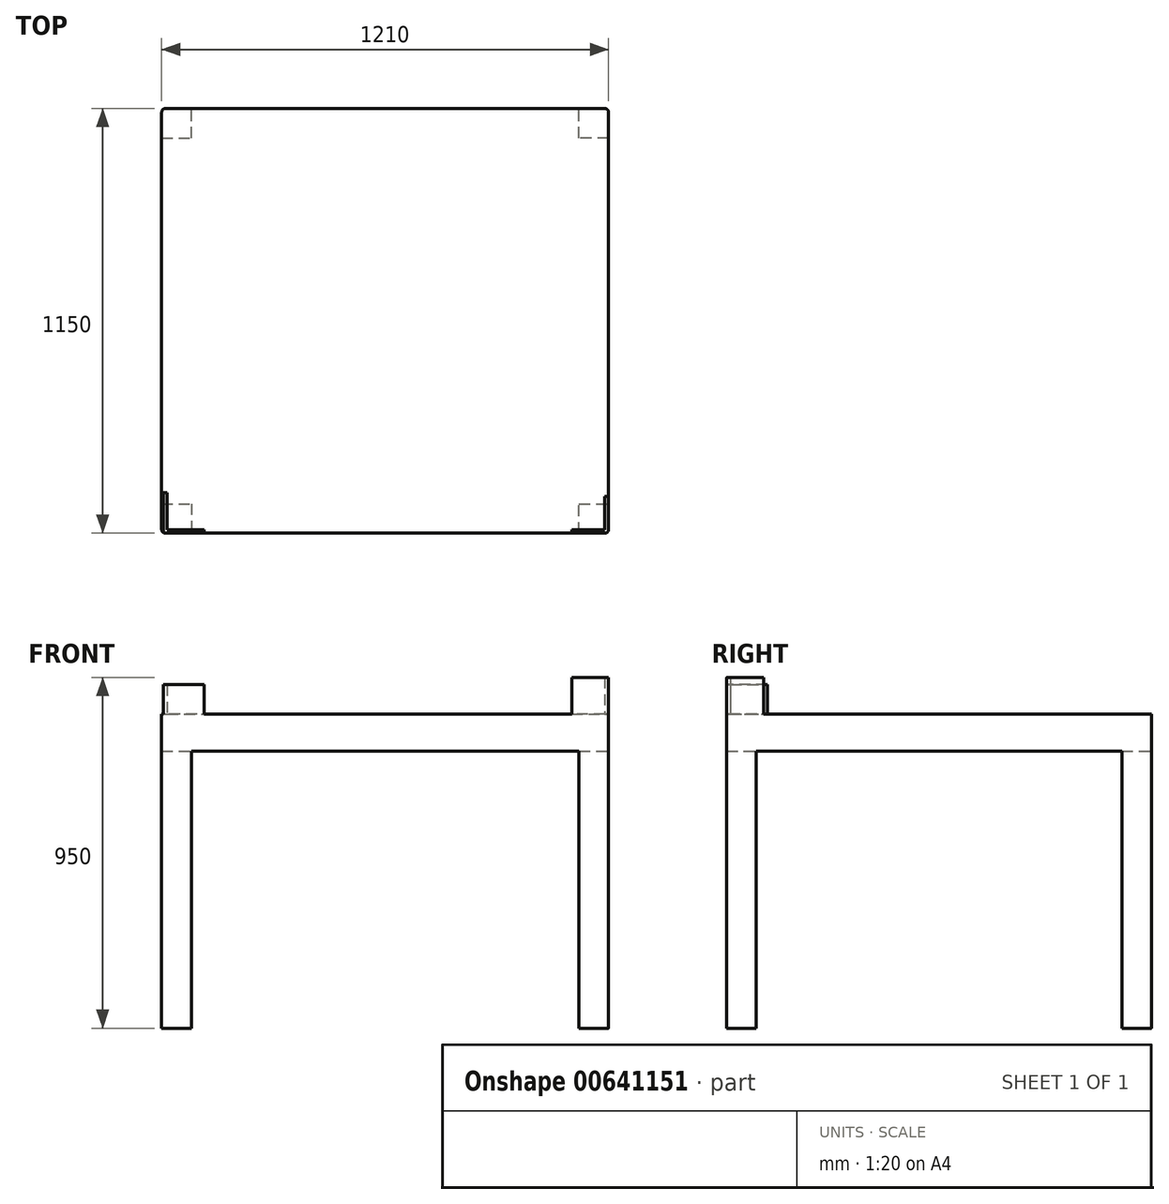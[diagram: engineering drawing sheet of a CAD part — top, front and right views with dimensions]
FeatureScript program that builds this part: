
annotation { "Feature Type Name" : "Feature", "Feature Type Description" : "" }
export const myFeature = defineFeature(function(context is Context, id is Id, definition is map)
    precondition{}
    {
        {
            var Q0;
            Q0=qCreatedBy(makeId("Top.planeOp"),FACE);
            var sketch = newSketch(context, id + "F0", { "sketchPlane" : qUnion([Q0])});
            skLineSegment(sketch, "E0.bottom", {"start": v(595, 575) * mm, "end": v(-595, 575) * mm});
            skLineSegment(sketch, "E0.top", {"start": v(595, -575) * mm, "end": v(-595, -575) * mm});
            skLineSegment(sketch, "E0.left", {"start": v(605, 565) * mm, "end": v(605, -565) * mm});
            skLineSegment(sketch, "E0.right", {"start": v(-605, 565) * mm, "end": v(-605, -565) * mm});
            skPoint(sketch, "E0.middle", {"position": v(0, 0) * mm});
            skPoint(sketch, "E1.visualSharp", {"position": v(-605, -575) * mm});
            skArc(sketch, "E1.filletArc", {"start": v(-605, -565) * mm, "mid": v(-602.07, -572.07) * mm, "end": v(-595, -575) * mm});
            skPoint(sketch, "E2.visualSharp", {"position": v(605, -575) * mm});
            skArc(sketch, "E2.filletArc", {"start": v(595, -575) * mm, "mid": v(602.07, -572.07) * mm, "end": v(605, -565) * mm});
            skPoint(sketch, "E3.visualSharp", {"position": v(605, 575) * mm});
            skArc(sketch, "E3.filletArc", {"start": v(605, 565) * mm, "mid": v(602.07, 572.07) * mm, "end": v(595, 575) * mm});
            skPoint(sketch, "E4.visualSharp", {"position": v(-605, 575) * mm});
            skArc(sketch, "E4.filletArc", {"start": v(-595, 575) * mm, "mid": v(-602.07, 572.07) * mm, "end": v(-605, 565) * mm});
            skSolve(sketch);
        }
        {
            var Q0;
            Q0=makeQuery(id+"F0.imprint","IMPRINT",FACE,{"disambiguationData":[TD([[makeQuery(id+"F0.imprint","IMPRINT",EDGE,{"derivedFrom":sQuery(id+"F0.wireOp",EDGE,"E0.bottom")}),1.0]])]});
            extrude(context, id + "F1", {"entities" : qUnion([Q0]), "depth" : 80 * mm, "offsetDistance" : 25 * mm});
        }
        {
            var Q0;
            Q0=makeQuery(id+"F1.opExtrude","CAP_FACE",FACE,{"disambiguationData":[OSD([sQuery(id+"F0.wireOp",EDGE,"E0.bottom"),sQuery(id+"F0.wireOp",EDGE,"E0.top"),sQuery(id+"F0.wireOp",EDGE,"E0.left"),sQuery(id+"F0.wireOp",EDGE,"E0.right")])],"isStart":false});
            var sketch = newSketch(context, id + "F2", { "sketchPlane" : qUnion([Q0])});
            skLineSegment(sketch, "E5", {"start": v(-600, -575) * mm, "end": v(-490, -575) * mm});
            skLineSegment(sketch, "E6", {"start": v(-490, -575) * mm, "end": v(-490, -565) * mm});
            skLineSegment(sketch, "E7", {"start": v(-490, -565) * mm, "end": v(-590, -565) * mm});
            skLineSegment(sketch, "E8", {"start": v(-590, -565) * mm, "end": v(-590, -465) * mm});
            skLineSegment(sketch, "E9", {"start": v(-590, -465) * mm, "end": v(-600, -465) * mm});
            skLineSegment(sketch, "E10", {"start": v(-600, -465) * mm, "end": v(-600, -575) * mm});
            skSolve(sketch);
        }
        {
            var Q0;
            Q0=makeQuery(id+"F2.imprint","IMPRINT",FACE,{"disambiguationData":[TD([[makeQuery(id+"F2.imprint","IMPRINT",EDGE,{"derivedFrom":sQuery(id+"F2.wireOp",EDGE,"E5")}),-1.0]])]});
            var Q1;
            Q1=makeQuery(id+"F1.opExtrude","CAP_FACE",FACE,{"disambiguationData":[OSD([sQuery(id+"F0.wireOp",EDGE,"E0.bottom"),sQuery(id+"F0.wireOp",EDGE,"E0.top"),sQuery(id+"F0.wireOp",EDGE,"E0.left"),sQuery(id+"F0.wireOp",EDGE,"E0.right")])],"isStart":true});
            extrude(context, id + "F3", {"entities" : qUnion([Q0, Q1]), "operationType" : NewBodyOperationType.ADD, "depth" : 100 * mm, "offsetDistance" : 25 * mm});
        }
        {
            var Q0;
            Q0=makeQuery(id+"F3.opExtrude","CAP_FACE",FACE,{"disambiguationData":[OSD([sQuery(id+"F0.wireOp",EDGE,"E0.bottom"),sQuery(id+"F0.wireOp",EDGE,"E0.top"),sQuery(id+"F0.wireOp",EDGE,"E0.left"),sQuery(id+"F0.wireOp",EDGE,"E0.right"),sQuery(id+"F0.wireOp",EDGE,"E1.filletArc"),sQuery(id+"F0.wireOp",EDGE,"E2.filletArc"),sQuery(id+"F0.wireOp",EDGE,"E3.filletArc"),sQuery(id+"F0.wireOp",EDGE,"E4.filletArc")])],"isStart":false});
            var sketch = newSketch(context, id + "F4", { "sketchPlane" : qUnion([Q0])});
            skLineSegment(sketch, "E11", {"start": v(505, -575) * mm, "end": v(505, -565) * mm});
            skLineSegment(sketch, "E12", {"start": v(505, -565) * mm, "end": v(595, -565) * mm});
            skLineSegment(sketch, "E13", {"start": v(595, -565) * mm, "end": v(595, -475) * mm});
            skLineSegment(sketch, "E14", {"start": v(595, -475) * mm, "end": v(605, -475) * mm});
            skSolve(sketch);
        }
        {
            var Q0;
            {var subQ3=sQuery(id+"F4.wireOp",EDGE,"E11");Q0=makeQuery(id+"F4.imprint","IMPRINT",FACE,{"disambiguationData":[TD([[makeQuery(id+"F4.imprint","IMPRINT",EDGE,{"derivedFrom":subQ3}),-1.0]])]});}
            extrude(context, id + "F5", {"entities" : qUnion([Q0]), "operationType" : NewBodyOperationType.ADD, "depth" : 100 * mm, "offsetDistance" : 25 * mm});
        }
        {
            var Q0;
            Q0=makeQuery(id+"F1.opExtrude","CAP_FACE",FACE,{"disambiguationData":[OSD([sQuery(id+"F0.wireOp",EDGE,"E0.bottom"),sQuery(id+"F0.wireOp",EDGE,"E0.top"),sQuery(id+"F0.wireOp",EDGE,"E0.left"),sQuery(id+"F0.wireOp",EDGE,"E0.right"),sQuery(id+"F0.wireOp",EDGE,"E1.filletArc"),sQuery(id+"F0.wireOp",EDGE,"E2.filletArc"),sQuery(id+"F0.wireOp",EDGE,"E3.filletArc"),sQuery(id+"F0.wireOp",EDGE,"E4.filletArc")])],"isStart":true});
            var sketch = newSketch(context, id + "F6", { "sketchPlane" : qUnion([Q0])});
            skLineSegment(sketch, "E15", {"start": v(-605, 495) * mm, "end": v(-525, 495) * mm});
            skLineSegment(sketch, "E16", {"start": v(-525, 495) * mm, "end": v(-525, 575) * mm});
            skLineSegment(sketch, "E17", {"start": v(525, 575) * mm, "end": v(525, 495) * mm});
            skLineSegment(sketch, "E18", {"start": v(525, 495) * mm, "end": v(605, 495) * mm});
            skLineSegment(sketch, "E19", {"start": v(-605, -495) * mm, "end": v(-525, -495) * mm});
            skLineSegment(sketch, "E20", {"start": v(605, -495) * mm, "end": v(525, -495) * mm});
            skLineSegment(sketch, "E21", {"start": v(525, -495) * mm, "end": v(525, -575) * mm});
            skLineSegment(sketch, "E22", {"start": v(-525, -495) * mm, "end": v(-525, -575) * mm});
            skSolve(sketch);
        }
        {
            var Q0;
            {var subQ3=sQuery(id+"F6.wireOp",EDGE,"E15");Q0=makeQuery(id+"F6.imprint","IMPRINT",FACE,{"disambiguationData":[TD([[makeQuery(id+"F6.imprint","IMPRINT",EDGE,{"derivedFrom":subQ3}),1.0]])]});}
            var Q1;
            {var subQ3=sQuery(id+"F6.wireOp",EDGE,"E19");Q1=makeQuery(id+"F6.imprint","IMPRINT",FACE,{"disambiguationData":[TD([[makeQuery(id+"F6.imprint","IMPRINT",EDGE,{"derivedFrom":subQ3}),-1.0]])]});}
            var Q2;
            {var subQ3=sQuery(id+"F6.wireOp",EDGE,"E20");Q2=makeQuery(id+"F6.imprint","IMPRINT",FACE,{"disambiguationData":[TD([[makeQuery(id+"F6.imprint","IMPRINT",EDGE,{"derivedFrom":subQ3}),1.0]])]});}
            var Q3;
            {var subQ2=sQuery(id+"F6.wireOp",EDGE,"E17");Q3=makeQuery(id+"F6.imprint","IMPRINT",FACE,{"disambiguationData":[TD([[makeQuery(id+"F6.imprint","IMPRINT",EDGE,{"derivedFrom":subQ2}),1.0]])]});}
            extrude(context, id + "F7", {"entities" : qUnion([Q0, Q1, Q2, Q3]), "operationType" : NewBodyOperationType.ADD, "depth" : 750 * mm, "offsetDistance" : 25 * mm});
        }
    });
